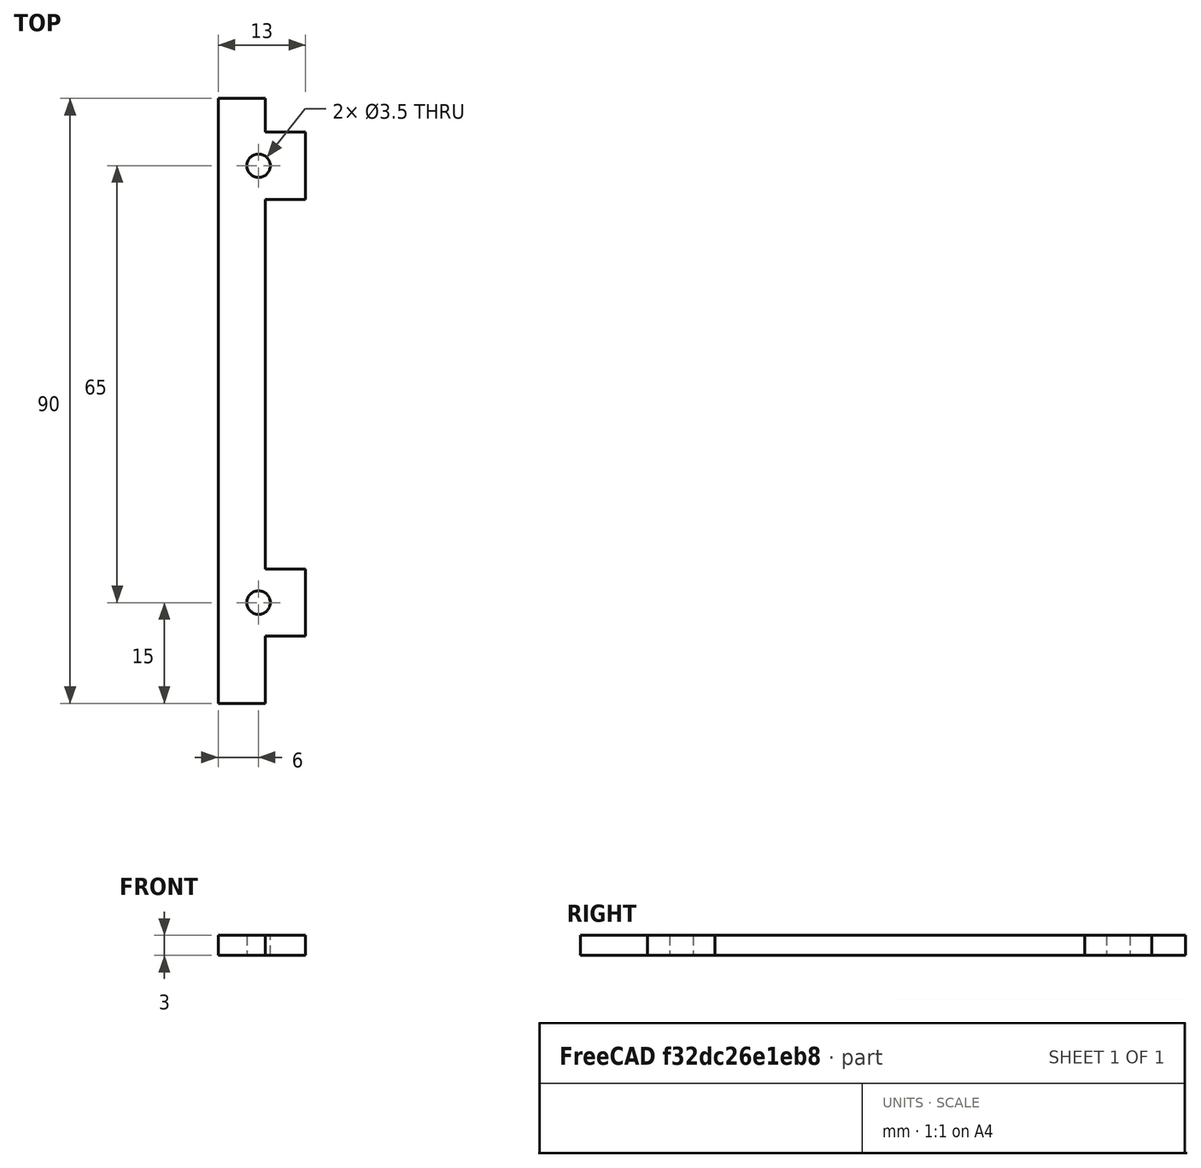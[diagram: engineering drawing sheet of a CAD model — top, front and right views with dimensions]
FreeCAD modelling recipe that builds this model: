
FCSTD DOCUMENT  (FreeCAD 0.18R)
Label: K-MINI-Enclosure-InnerWall
License: CreativeCommons Attribution
LicenseURL: http://creativecommons.org/licenses/by/4.0/
objects: Sketcher::SketchObject×5, PartDesign::Pocket×3, PartDesign::Pad×2, PartDesign::Fillet×1, PartDesign::Body×1, App::Part×1, Mesh::Feature×1
note: 17 computed .brp shape members not serialized (recipe doc carries the construction recipe); baked Part::Feature solids carry a one-line shape summary decoded from their .brp

FEATURE [Sketcher::SketchObject] Sketch  label="BaseProfile"
  MapMode = 5
  Support = -> [XY_Plane]
  sketch-geometry (14):
    g0: LineSegment StartX=4 StartY=90 StartZ=0 EndX=4 EndY=0 EndZ=0
    g1: LineSegment StartX=17 StartY=75 StartZ=0 EndX=17 EndY=85 EndZ=0
    g2: LineSegment StartX=11 StartY=75 StartZ=0 EndX=11 EndY=20 EndZ=0
    g3: LineSegment StartX=11 StartY=0 StartZ=0 EndX=4 EndY=0 EndZ=0
    g4: Circle CenterX=10 CenterY=80 CenterZ=0 NormalX=0 NormalY=0 NormalZ=1 AngleXU=0 Radius=1.75
    g5: LineSegment StartX=11 StartY=75 StartZ=0 EndX=17 EndY=75 EndZ=0
    g6: LineSegment StartX=11 StartY=20 StartZ=0 EndX=17 EndY=20 EndZ=0
    g7: LineSegment StartX=17 StartY=20 StartZ=0 EndX=17 EndY=10 EndZ=0
    g8: Circle CenterX=10 CenterY=15 CenterZ=0 NormalX=0 NormalY=0 NormalZ=1 AngleXU=0 Radius=1.75
    g9: LineSegment StartX=11 StartY=0 StartZ=0 EndX=11 EndY=10 EndZ=0
    g10: LineSegment StartX=11 StartY=10 StartZ=0 EndX=17 EndY=10 EndZ=0
    g11: LineSegment StartX=4 StartY=90 StartZ=0 EndX=11 EndY=90 EndZ=0
    g12: LineSegment StartX=11 StartY=90 StartZ=0 EndX=11 EndY=85 EndZ=0
    g13: LineSegment StartX=11 StartY=85 StartZ=0 EndX=17 EndY=85 EndZ=0
  constraints (42):
    c: Vertical(g0)
    c: Vertical(g1)
    c: Horizontal(g3)
    c: Vertical(g2)
    c: PointOnObject(g0,g-1)
    c: Coincident(g0,g3)
    c: DistanceX(g-1,g0) = 4
    c: Radius(g4) = 1.75
    c: DistanceX(g-1,g4) = 10
    c: Coincident(g2,g5)
    c: Horizontal(g5)
    c: Coincident(g5,g1)
    c: Coincident(g6,g7)
    c: Horizontal(g6)
    c: Vertical(g7)
    c: Coincident(g2,g6)
    c: DistanceX(g0,g2) = 7
    c: Vertical(g1,g6)
    c: Radius(g8) = 1.75
    c: Vertical(g4,g8)
    c: DistanceY(g-1,g8) = 15
    c: DistanceY(g-1,g2) = 20
    c: Coincident(g9,g10)
    c: Coincident(g7,g10)
    c: Vertical(g9)
    c: Horizontal(g10)
    c: Coincident(g3,g9)
    c: Vertical(g2,g9)
    c: Coincident(g11,g12)
    c: Coincident(g12,g13)
    c: Coincident(g1,g13)
    c: Coincident(g0,g11)
    c: DistanceY(g-1,g0) = 90
    c: Horizontal(g11)
    c: Horizontal(g13)
    c: Vertical(g12)
    c: DistanceY(g4,g0) = 10
    c: Vertical(g2,g12)
    c: DistanceY(g7,g7) = 10
    c: DistanceY(g1,g1) = 10
    c: DistanceY(g4,g1) = 5
    c: DistanceX(g4,g1) = 7
FEATURE [PartDesign::Pad] Pad  label="Base"
  Length = 3
  Length2 = 100
  Profile = -> Sketch
  Type = 0
FEATURE [Sketcher::SketchObject] Sketch001  label="WallProfile"
  MapMode = 5
  Placement = pos=(0,0,3) rot=(0,0,1;0rad)
  Support = -> [Pad]
  sketch-geometry (12):
    g0: LineSegment StartX=6 StartY=0 StartZ=0 EndX=6 EndY=21 EndZ=0
    g1: LineSegment StartX=6 StartY=29 StartZ=0 EndX=6 EndY=61 EndZ=0
    g2: LineSegment StartX=4 StartY=90 StartZ=0 EndX=4 EndY=0 EndZ=0
    g3: LineSegment StartX=4 StartY=0 StartZ=0 EndX=6 EndY=0 EndZ=0
    g4: LineSegment StartX=6 StartY=61 StartZ=0 EndX=16 EndY=61 EndZ=0
    g5: LineSegment StartX=16 StartY=61 StartZ=0 EndX=16 EndY=69 EndZ=0
    g6: LineSegment StartX=16 StartY=69 StartZ=0 EndX=6 EndY=69 EndZ=0
    g7: LineSegment StartX=6 StartY=69 StartZ=0 EndX=6 EndY=90 EndZ=0
    g8: LineSegment StartX=6 StartY=90 StartZ=0 EndX=4 EndY=90 EndZ=0
    g9: LineSegment StartX=6 StartY=29 StartZ=0 EndX=16 EndY=29 EndZ=0
    g10: LineSegment StartX=16 StartY=29 StartZ=0 EndX=16 EndY=21 EndZ=0
    g11: LineSegment StartX=16 StartY=21 StartZ=0 EndX=6 EndY=21 EndZ=0
  constraints (36):
    c: Vertical(g1)
    c: Vertical(g2)
    c: Horizontal(g3)
    c: Coincident(g0,g3)
    c: Coincident(g2,g3)
    c: PointOnObject(g2,g-1)
    c: DistanceX(g-1,g2) = 4
    c: DistanceX(g3,g3) = 2
    c: Vertical(g0)
    c: Coincident(g7,g8)
    c: Horizontal(g8)
    c: Horizontal(g6)
    c: Horizontal(g4)
    c: Vertical(g5)
    c: DistanceX(g8,g8) = 2
    c: Vertical(g7)
    c: DistanceY(g0,g8) = 90
    c: Coincident(g2,g8)
    c: Coincident(g5,g6)
    c: Coincident(g4,g5)
    c: Coincident(g6,g7)
    c: Coincident(g1,g4)
    c: Coincident(g9,g10)
    c: Coincident(g10,g11)
    c: Coincident(g0,g11)
    c: Coincident(g1,g9)
    c: Horizontal(g9)
    c: Horizontal(g11)
    c: Vertical(g10)
    c: Vertical(g1,g0)
    c: Vertical(g4,g9)
    c: DistanceX(g6,g6) = 10
    c: DistanceY(g5,g5) = 8
    c: DistanceY(g10,g10) = 8
    c: DistanceY(g-1,g0) = 21
    c: DistanceY(g0,g1) = 40
FEATURE [Sketcher::SketchObject] Sketch003  label="Coroplast Profile"
  AttachmentOffset = pos=(0,0,54) rot=(0,0,1;0rad)
  MapMode = 5
  Placement = pos=(0,0,54) rot=(0,0,1;0rad)
  Support = -> [XY_Plane]
  sketch-geometry (4):
    g0: LineSegment StartX=6 StartY=115 StartZ=0 EndX=6 EndY=-40 EndZ=0
    g1: LineSegment StartX=6 StartY=-40 StartZ=0 EndX=149.495 EndY=-40 EndZ=0
    g2: LineSegment StartX=149.495 StartY=-40 StartZ=0 EndX=149.495 EndY=115 EndZ=0
    g3: LineSegment StartX=149.495 StartY=115 StartZ=0 EndX=6 EndY=115 EndZ=0
  constraints (10):
    c: Coincident(g0,g1)
    c: Coincident(g2,g3)
    c: Vertical(g2)
    c: Vertical(g0)
    c: Horizontal(g1)
    c: Horizontal(g3)
    c: Coincident(g0,g3)
    c: DistanceX(g-1,g0) = 6
    c: Coincident(g1,g2)
    c: DistanceY(g1,g-1) = 40
FEATURE [PartDesign::Pad] Pad001  label="Wall"
  BaseFeature = -> Pad
  Length = 54
  Length2 = 100
  Profile = -> Sketch001
  Type = 0
FEATURE [PartDesign::Pocket] Pocket  label="CoroHCutout"
  BaseFeature = -> Pad001
  Length = 3
  Length2 = 100
  Profile = -> Sketch003
  Reversed = true
  Type = 0
FEATURE [Sketcher::SketchObject] Sketch004  label="CoroSupportProfile"
  MapMode = 5
  Placement = pos=(0,69,0) rot=(0,0.707107,0.707107;3.14159rad)
  Support = -> [Pocket]
  sketch-geometry (4):
    g0: LineSegment StartX=-7 StartY=3 StartZ=0 EndX=-7 EndY=33 EndZ=0
    g1: LineSegment StartX=-7 StartY=33 StartZ=0 EndX=-17 EndY=48 EndZ=0
    g2: LineSegment StartX=-17 StartY=48 StartZ=0 EndX=-17 EndY=3 EndZ=0
    g3: LineSegment StartX=-17 StartY=3 StartZ=0 EndX=-7 EndY=3 EndZ=0
  constraints (12):
    c: Coincident(g0,g1)
    c: Coincident(g2,g3)
    c: Coincident(g0,g3)
    c: Horizontal(g3)
    c: Vertical(g2)
    c: Vertical(g0)
    c: DistanceY(g-1,g2) = 3
    c: DistanceX(g0,g-1) = 7
    c: Coincident(g2,g1)
    c: DistanceY(g0,g0) = 30
    c: DistanceY(g2,g2) = 45
    c: DistanceX(g3,g3) = 10
FEATURE [PartDesign::Pocket] Pocket001  label="CoroSupportV"
  BaseFeature = -> Pocket
  Length = 50
  Length2 = 100
  Profile = -> Sketch004
  Type = 0
FEATURE [Sketcher::SketchObject] Sketch005  label="CoroMountHolePos"
  MapMode = 5
  Placement = pos=(0,0,57) rot=(0,0,1;0rad)
  Support = -> [Pocket001]
  sketch-geometry (2):
    g0: Circle CenterX=12 CenterY=65 CenterZ=0 NormalX=0 NormalY=0 NormalZ=1 AngleXU=0 Radius=1.3
    g1: Circle CenterX=12 CenterY=25 CenterZ=0 NormalX=0 NormalY=0 NormalZ=1 AngleXU=0 Radius=1.3
  constraints (6):
    c: DistanceY(g-1,g0) = 65
    c: DistanceX(g-1,g0) = 12
    c: Radius(g0) = 1.3
    c: Radius(g1) = 1.3
    c: Vertical(g0,g1)
    c: DistanceY(g1,g0) = 40
FEATURE [PartDesign::Pocket] Pocket002  label="CoroMountHoles"
  BaseFeature = -> Pocket001
  Length = 13
  Length2 = 100
  Profile = -> Sketch005
  Type = 0
FEATURE [PartDesign::Fillet] Fillet
  Base = -> Pocket002 [Edge26]
  BaseFeature = -> Pocket002
  Radius = 1.5
FEATURE [PartDesign::Body] Body  label="InnerWall"
  Group = -> [Sketch,Pad,Sketch001,Sketch003,Pad001,Pocket,Pocket001,Pocket002,Fillet,Sketch005,Sketch004]
  Origin = -> Origin
  Tip = -> Pad
FEATURE [App::Part] Part
  Group = -> [Body]
  Origin = -> Origin001
FEATURE [Mesh::Feature] Mesh  label="Fillet (Meshed)"
